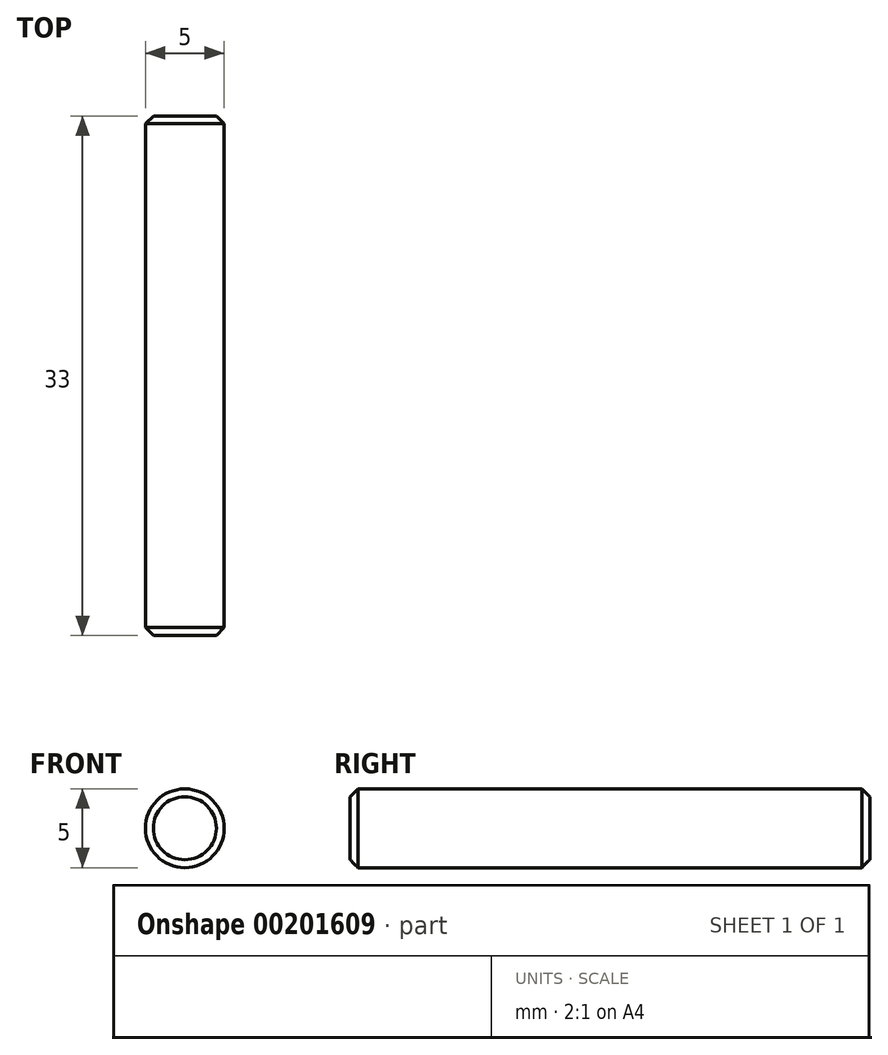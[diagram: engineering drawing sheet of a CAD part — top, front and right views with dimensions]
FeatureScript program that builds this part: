
annotation { "Feature Type Name" : "Feature", "Feature Type Description" : "" }
export const myFeature = defineFeature(function(context is Context, id is Id, definition is map)
    precondition{}
    {
        {
            var Q0;
            Q0=qCreatedBy(makeId("Front.planeOp"),FACE);
            var sketch = newSketch(context, id + "F0", { "sketchPlane" : qUnion([Q0])});
            skCircle(sketch, "E0", {"center": v(0, 0) * mm, "radius": 2.5 * mm});
            skSolve(sketch);
        }
        {
            var Q0;
            Q0=makeQuery(id+"F0.imprint","IMPRINT",FACE,{"disambiguationData":[TD([[makeQuery(id+"F0.imprint","IMPRINT",EDGE,{"derivedFrom":sQuery(id+"F0.wireOp",EDGE,"E0")}),1.0]])]});
            extrude(context, id + "F1", {"entities" : qUnion([Q0]), "depth" : 33 * mm});
        }
        {
            var Q0;
            Q0=makeQuery(id+"F1.opExtrude","CAP_EDGE",EDGE,{"disambiguationData":[OSD([sQuery(id+"F0.wireOp",EDGE,"E0")])],"isStart":false});
            var Q1;
            Q1=makeQuery(id+"F1.opExtrude","CAP_EDGE",EDGE,{"disambiguationData":[OSD([sQuery(id+"F0.wireOp",EDGE,"E0")])],"isStart":true});
            chamfer(context, id + "F2", {"entities" : qUnion([Q0, Q1]), "width" : .5 * mm, "tangentPropagation" : true});
        }
    });
